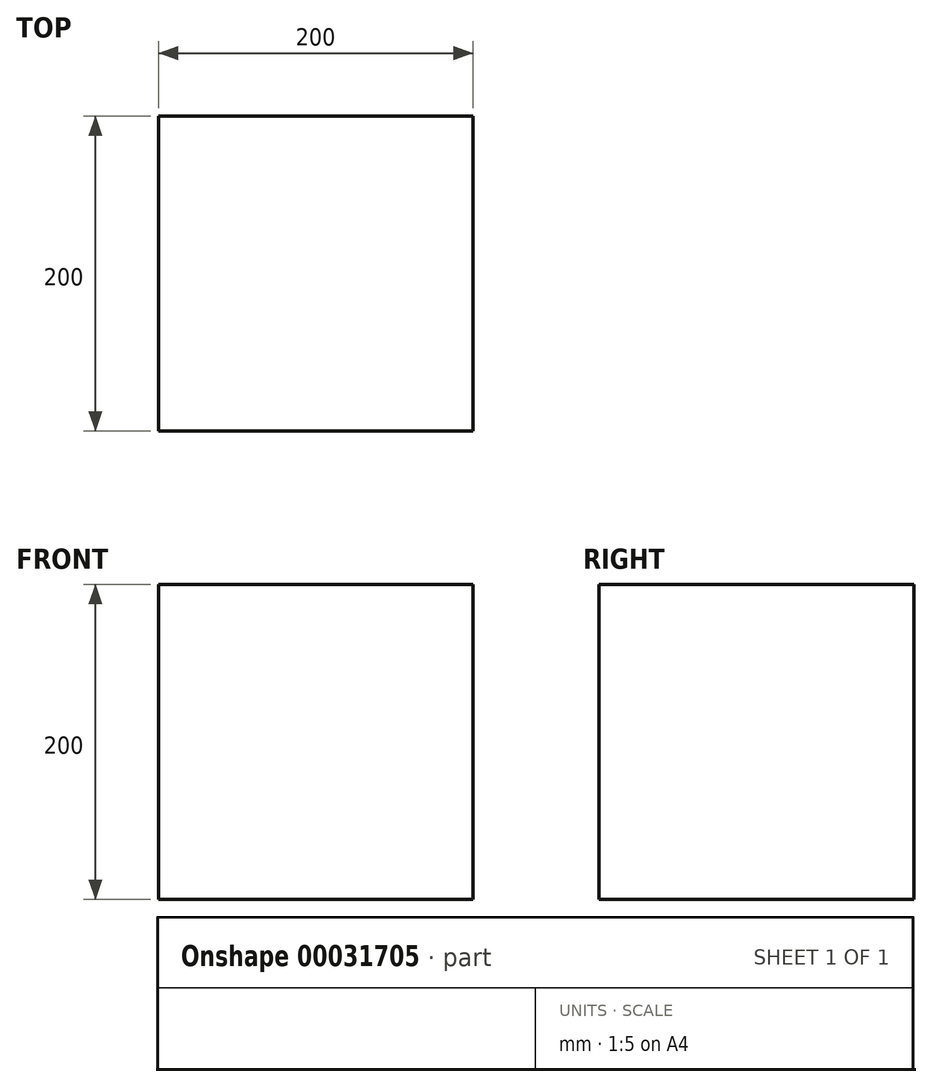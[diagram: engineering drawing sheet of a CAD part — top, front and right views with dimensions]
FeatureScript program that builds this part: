
annotation { "Feature Type Name" : "Feature", "Feature Type Description" : "" }
export const myFeature = defineFeature(function(context is Context, id is Id, definition is map)
    precondition{}
    {
        {
            var Q0;
            Q0=qCreatedBy(makeId("Top.planeOp"),FACE);
            var sketch = newSketch(context, id + "F0", { "sketchPlane" : qUnion([Q0])});
            skLineSegment(sketch, "E0.bottom", {"start": v(0, 0) * mm, "end": v(200, 0) * mm});
            skLineSegment(sketch, "E0.top", {"start": v(0, 200) * mm, "end": v(200, 200) * mm});
            skLineSegment(sketch, "E0.left", {"start": v(0, 0) * mm, "end": v(0, 200) * mm});
            skLineSegment(sketch, "E0.right", {"start": v(200, 0) * mm, "end": v(200, 200) * mm});
            skSolve(sketch);
        }
        {
            var Q0;
            Q0 = qSketchRegion(id + "F0", true);
            extrude(context, id + "F1", {"entities" : qUnion([Q0]), "depth" : 200 * mm});
        }
    });
